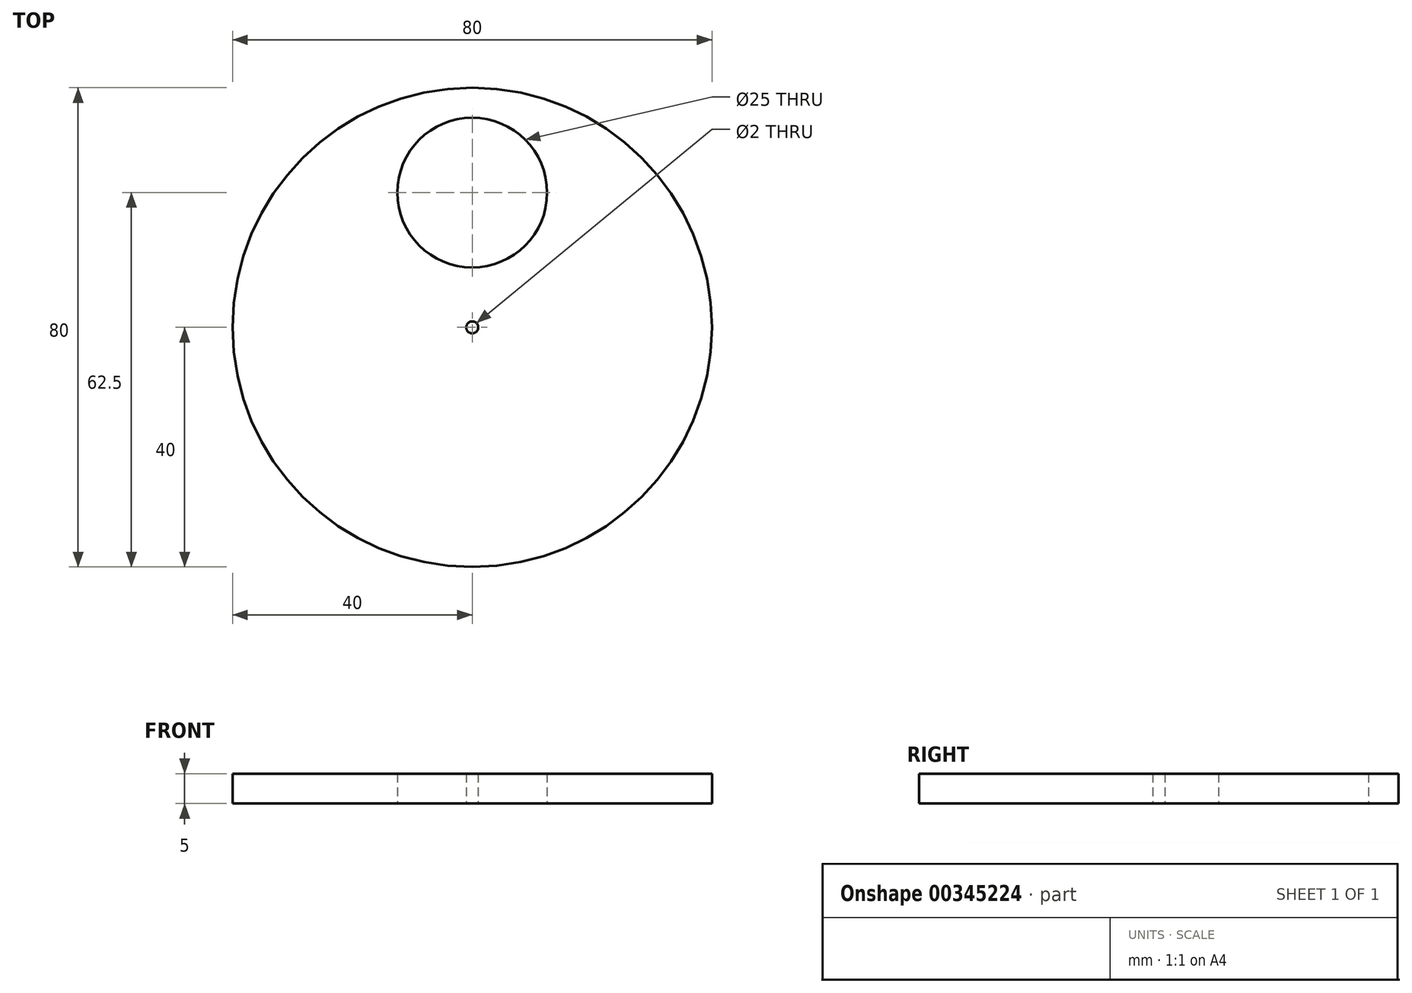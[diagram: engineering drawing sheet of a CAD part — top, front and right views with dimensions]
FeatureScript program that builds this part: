
annotation { "Feature Type Name" : "Feature", "Feature Type Description" : "" }
export const myFeature = defineFeature(function(context is Context, id is Id, definition is map)
    precondition{}
    {
        {
            var Q0;
            Q0=qCreatedBy(makeId("Top.planeOp"),FACE);
            var sketch = newSketch(context, id + "F0", { "sketchPlane" : qUnion([Q0])});
            skCircle(sketch, "E0", {"center": v(0, 0) * mm, "radius": 40 * mm});
            skCircle(sketch, "E1", {"center": v(0, 22.5) * mm, "radius": 12.5 * mm});
            skCircle(sketch, "E2", {"center": v(0, 0) * mm, "radius": 1 * mm});
            skSolve(sketch);
        }
        {
            var Q0;
            Q0=makeQuery(id+"F0.imprint","IMPRINT",FACE,{"disambiguationData":[TD([[makeQuery(id+"F0.imprint","IMPRINT",EDGE,{"derivedFrom":sQuery(id+"F0.wireOp",EDGE,"E0")}),1.0]])]});
            extrude(context, id + "F1", {"entities" : qUnion([Q0]), "depth" : 5 * mm});
        }
    });
